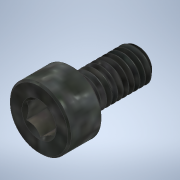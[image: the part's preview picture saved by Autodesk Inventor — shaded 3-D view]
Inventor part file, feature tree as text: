
AUTODESK INVENTOR PART (.ipt)
format: ipt  version: 2020.5 (Build 245400000, 400)  size: 425,472 bytes
history: native  units: in
note: dims shown in document units (in); Inventor stores cm internally (conversion verified against a paired STEP export)
features: revolve x1
ambient origin geometry x8: Origin, YZ Plane, XZ Plane, XY Plane, X Axis, Y Axis, Z Axis, Center Point
bodies: Solid1 (feature_tree)
feature tree (1):
  revolve  "Revolve2"  [1 undecoded]
note: 1 required parameter value undecoded (feature->parameter linkage not recoverable at this tier; creation-order binding heuristic only, values carry confidence <= 0.55)
